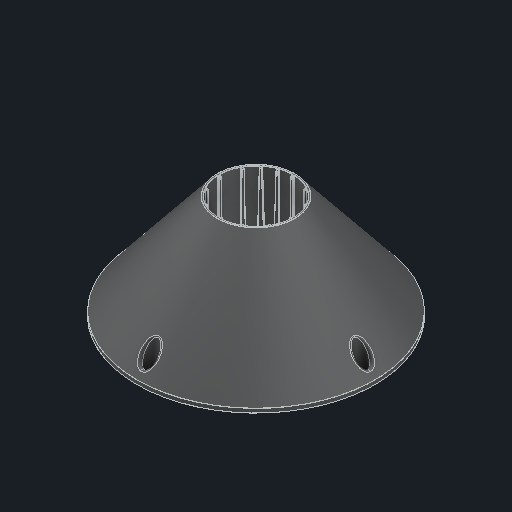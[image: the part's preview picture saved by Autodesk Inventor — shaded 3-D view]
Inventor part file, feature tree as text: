
AUTODESK INVENTOR PART (.ipt)
format: ipt  version: 2024.2 (Build 282272000, 272)  size: 3,985,920 bytes
history: native  units: in
note: dims shown in document units (in); Inventor stores cm internally (conversion verified against a paired STEP export)
features: fillet x1
ambient origin geometry x8: Origin, YZ Plane, XZ Plane, XY Plane, X Axis, Y Axis, Z Axis, Center Point
bodies: Solid1 (feature_tree)
feature tree (1):
  fillet  "Fillet22"  [1 undecoded]
note: 1 required parameter value undecoded (feature->parameter linkage not recoverable at this tier; creation-order binding heuristic only, values carry confidence <= 0.55)
